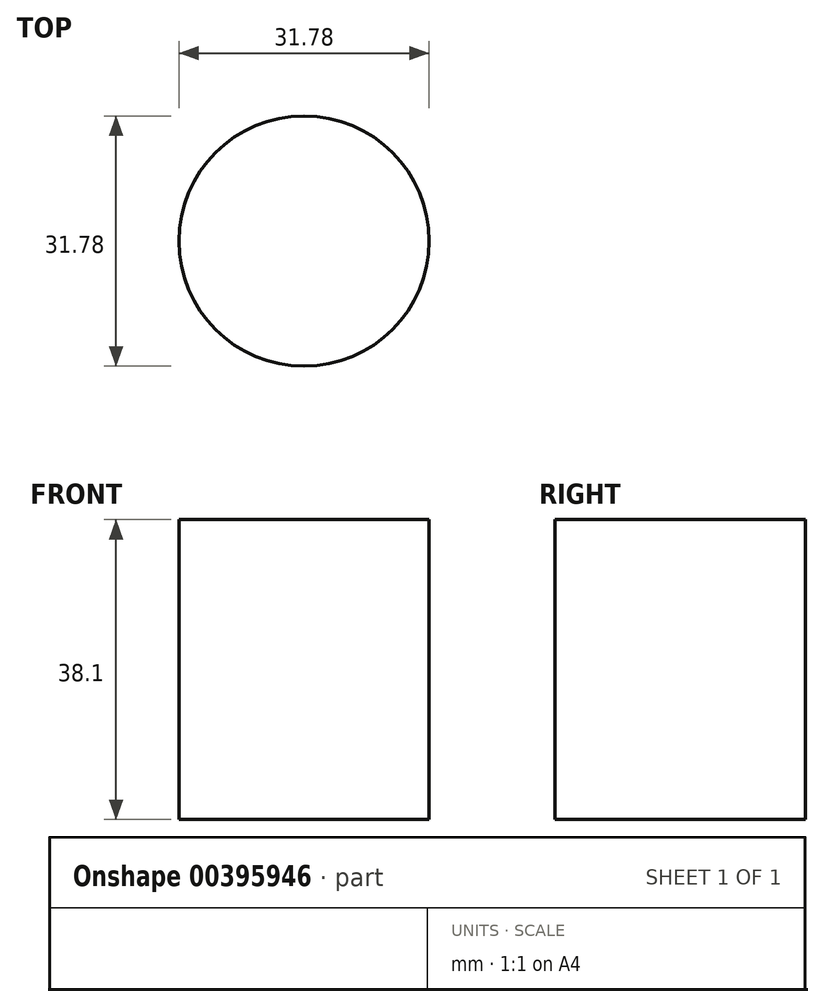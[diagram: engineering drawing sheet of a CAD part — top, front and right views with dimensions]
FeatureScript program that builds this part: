
annotation { "Feature Type Name" : "Feature", "Feature Type Description" : "" }
export const myFeature = defineFeature(function(context is Context, id is Id, definition is map)
    precondition{}
    {
        {
            var Q0;
            Q0=qCreatedBy(makeId("Top.planeOp"),FACE);
            var sketch = newSketch(context, id + "F0", { "sketchPlane" : qUnion([Q0])});
            skCircle(sketch, "E0", {"center": v(0, 0) * mm, "radius": 15.9 * mm});
            skSolve(sketch);
        }
        {
            var Q0;
            Q0=makeQuery(id+"F0.imprint","IMPRINT",FACE,{"disambiguationData":[TD([[makeQuery(id+"F0.imprint","IMPRINT",EDGE,{"derivedFrom":sQuery(id+"F0.wireOp",EDGE,"E0")}),1.0]])]});
            extrude(context, id + "F1", {"entities" : qUnion([Q0]), "depth" : 38.1 * mm});
        }
    });
